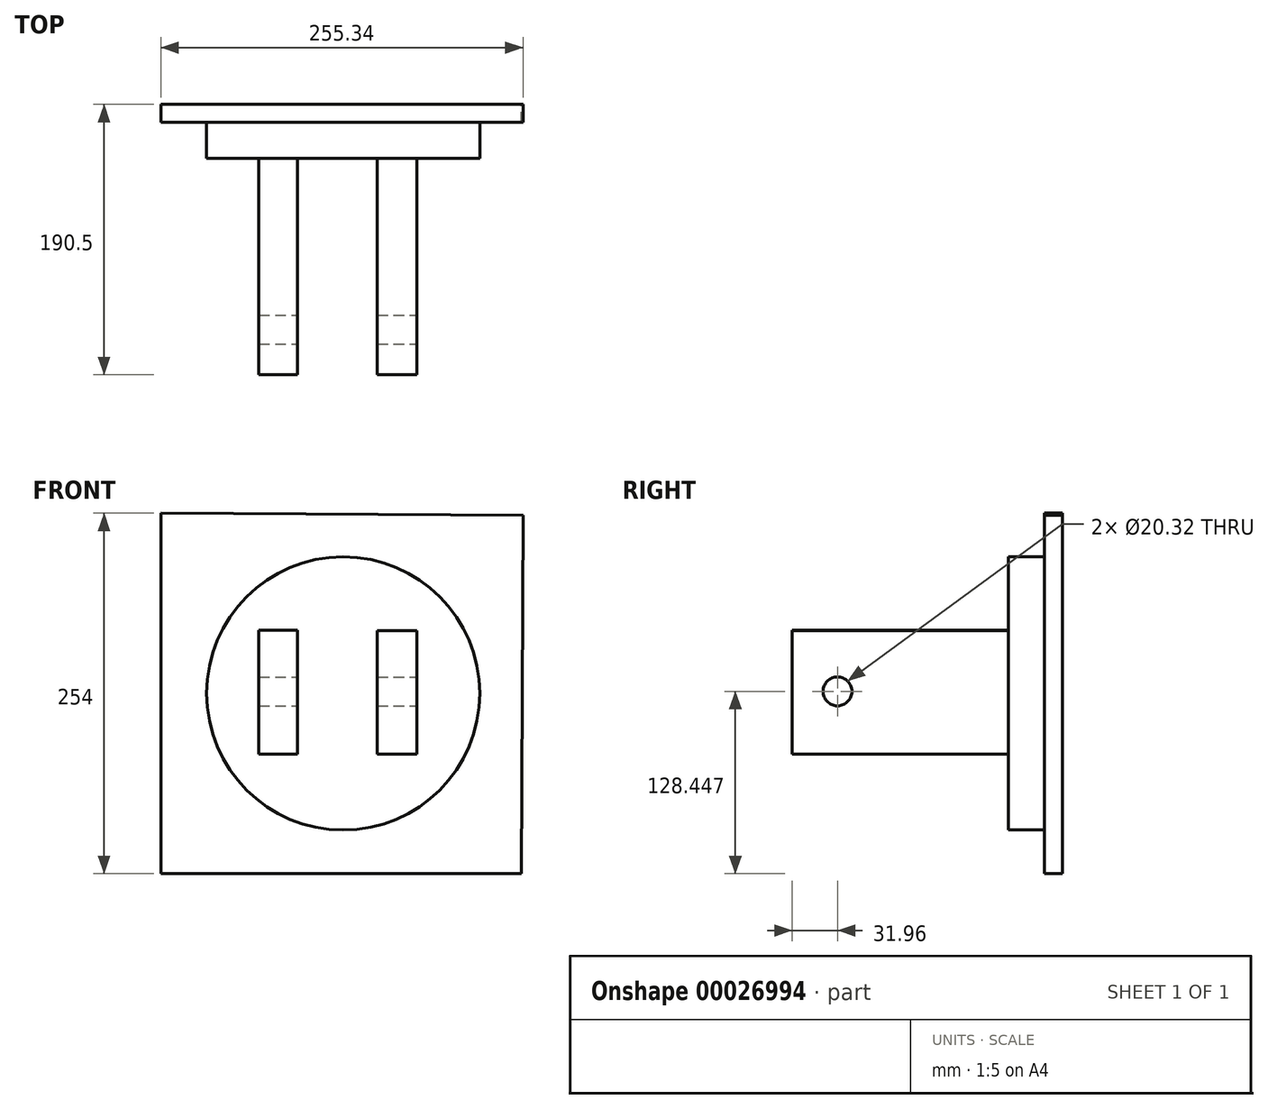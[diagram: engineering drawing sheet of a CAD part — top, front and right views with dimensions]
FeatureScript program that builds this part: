
annotation { "Feature Type Name" : "Feature", "Feature Type Description" : "" }
export const myFeature = defineFeature(function(context is Context, id is Id, definition is map)
    precondition{}
    {
        {
            var Q0;
            Q0=qCreatedBy(makeId("Front.planeOp"),FACE);
            var sketch = newSketch(context, id + "F0", { "sketchPlane" : qUnion([Q0])});
            skLineSegment(sketch, "E0", {"start": v(0, 0) * mm, "end": v(0, -254) * mm});
            skLineSegment(sketch, "E1", {"start": v(0, -254) * mm, "end": v(254, -254) * mm});
            skLineSegment(sketch, "E2", {"start": v(0, 0) * mm, "end": v(255.34, -1.36) * mm});
            skLineSegment(sketch, "E3", {"start": v(255.34, -1.36) * mm, "end": v(254, -254) * mm});
            skSolve(sketch);
        }
        {
            var Q0;
            Q0=makeQuery(id+"F0.imprint","IMPRINT",FACE,{"disambiguationData":[TD([[makeQuery(id+"F0.imprint","IMPRINT",EDGE,{"derivedFrom":sQuery(id+"F0.wireOp",EDGE,"E0")}),1.0]])]});
            extrude(context, id + "F1", {"entities" : qUnion([Q0]), "depth" : 12.7 * mm});
        }
        {
            var Q0;
            Q0=makeQuery(id+"F1.opExtrude","CAP_FACE",FACE,{"disambiguationData":[OSD([sQuery(id+"F0.wireOp",EDGE,"E0"),sQuery(id+"F0.wireOp",EDGE,"E1"),sQuery(id+"F0.wireOp",EDGE,"E2"),sQuery(id+"F0.wireOp",EDGE,"E3")])],"isStart":false});
            var sketch = newSketch(context, id + "F2", { "sketchPlane" : qUnion([Q0])});
            skCircle(sketch, "E4", {"center": v(128.54, -126.96) * mm, "radius": 96.23 * mm});
            skLineSegment(sketch, "E5", {"start": v(128.54, -126.96) * mm, "end": v(162.1, -126.96) * mm});
            skLineSegment(sketch, "E6", {"start": v(128.54, -126.96) * mm, "end": v(98.82, -126.96) * mm});
            skLineSegment(sketch, "E7", {"start": v(162.1, -126.96) * mm, "end": v(98.82, -126.96) * mm});
            skLineSegment(sketch, "E8", {"start": v(162.1, -126.96) * mm, "end": v(187.61, -126.96) * mm});
            skLineSegment(sketch, "E9", {"start": v(98.82, -126.96) * mm, "end": v(73.31, -126.96) * mm});
            skLineSegment(sketch, "E10", {"start": v(73.31, -126.96) * mm, "end": v(73.31, -158.25) * mm});
            skLineSegment(sketch, "E11", {"start": v(187.61, -126.96) * mm, "end": v(187.61, -158.25) * mm});
            skLineSegment(sketch, "E12", {"start": v(73.31, -158.25) * mm, "end": v(187.61, -158.25) * mm});
            skSolve(sketch);
        }
        {
            var Q0;
            Q0=makeQuery(id+"F2.imprint","IMPRINT",FACE,{"disambiguationData":[TD([[makeQuery(id+"F2.imprint","IMPRINT",EDGE,{"derivedFrom":sQuery(id+"F2.wireOp",EDGE,"E4")}),1.0]])]});
            var Q1;
            {var subQ1=sQuery(id+"F2.wireOp",EDGE,"E8");Q1=makeQuery(id+"F2.imprint","IMPRINT",FACE,{"disambiguationData":[TD([[makeQuery(id+"F2.imprint","IMPRINT",EDGE,{"derivedFrom":subQ1}),-1.0]])]});}
            extrude(context, id + "F3", {"entities" : qUnion([Q0, Q1]), "operationType" : NewBodyOperationType.ADD, "depth" : 25.4 * mm});
        }
        {
            var Q0;
            Q0=makeQuery(id+"F3.opExtrude","CAP_FACE",FACE,{"disambiguationData":[OSD([sQuery(id+"F2.wireOp",EDGE,"E4")])],"isStart":false});
            var sketch = newSketch(context, id + "F4", { "sketchPlane" : qUnion([Q0])});
            skLineSegment(sketch, "E13.bottom", {"start": v(69.16, -82.47) * mm, "end": v(96.16, -82.47) * mm});
            skLineSegment(sketch, "E13.top", {"start": v(69.16, -169.76) * mm, "end": v(96.16, -169.76) * mm});
            skLineSegment(sketch, "E13.left", {"start": v(69.16, -82.47) * mm, "end": v(69.16, -169.76) * mm});
            skLineSegment(sketch, "E13.right", {"start": v(96.16, -82.47) * mm, "end": v(96.16, -169.76) * mm});
            skLineSegment(sketch, "E14.bottom", {"start": v(152.5, -82.9) * mm, "end": v(180.33, -82.9) * mm});
            skLineSegment(sketch, "E14.top", {"start": v(152.5, -169.69) * mm, "end": v(180.33, -169.69) * mm});
            skLineSegment(sketch, "E14.left", {"start": v(152.5, -82.9) * mm, "end": v(152.5, -169.69) * mm});
            skLineSegment(sketch, "E15", {"start": v(180.33, -82.9) * mm, "end": v(180.33, -169.69) * mm});
            skSolve(sketch);
        }
        {
            var Q0;
            Q0=makeQuery(id+"F4.imprint","IMPRINT",FACE,{"disambiguationData":[TD([[makeQuery(id+"F4.imprint","IMPRINT",EDGE,{"derivedFrom":sQuery(id+"F4.wireOp",EDGE,"E13.bottom")}),-1.0]])]});
            var Q1;
            Q1=makeQuery(id+"F4.imprint","IMPRINT",FACE,{"disambiguationData":[TD([[makeQuery(id+"F4.imprint","IMPRINT",EDGE,{"derivedFrom":sQuery(id+"F4.wireOp",EDGE,"E14.bottom")}),-1.0]])]});
            extrude(context, id + "F5", {"entities" : qUnion([Q0, Q1]), "operationType" : NewBodyOperationType.ADD, "depth" : 152.4 * mm});
        }
        {
            var Q0;
            Q0=makeQuery(id+"F5.opExtrude","SWEPT_FACE",FACE,{"disambiguationData":[OSD([sQuery(id+"F4.wireOp",EDGE,"E15")])]});
            var sketch = newSketch(context, id + "F6", { "sketchPlane" : qUnion([Q0])});
            skCircle(sketch, "E16", {"center": v(-158.54, -125.55) * mm, "radius": 10.16 * mm});
            skSolve(sketch);
        }
        {
            var Q0;
            Q0=makeQuery(id+"F6.imprint","IMPRINT",FACE,{"disambiguationData":[TD([[makeQuery(id+"F6.imprint","IMPRINT",EDGE,{"derivedFrom":sQuery(id+"F6.wireOp",EDGE,"E16")}),1.0]])]});
            extrude(context, id + "F7", {"entities" : qUnion([Q0]), "operationType" : NewBodyOperationType.REMOVE, "endBound" : BoundingType.THROUGH_ALL, "oppositeDirection" : true, "depth" : 25.4 * mm});
        }
    });
